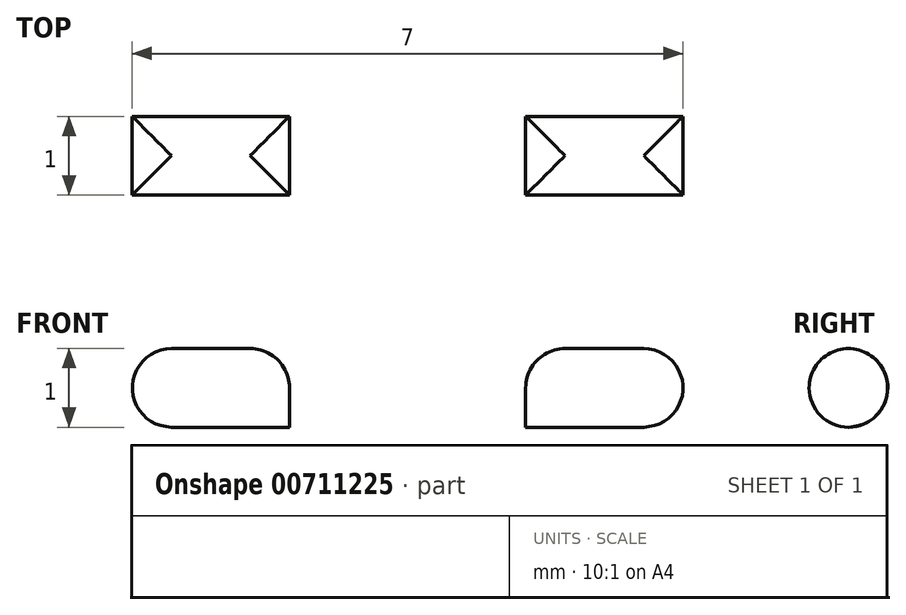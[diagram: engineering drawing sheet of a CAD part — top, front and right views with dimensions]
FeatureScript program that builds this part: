
annotation { "Feature Type Name" : "Feature", "Feature Type Description" : "" }
export const myFeature = defineFeature(function(context is Context, id is Id, definition is map)
    precondition{}
    {
        {
            var Q0;
            Q0=qCreatedBy(makeId("Top.planeOp"),FACE);
            var sketch = newSketch(context, id + "F0", { "sketchPlane" : qUnion([Q0])});
            skCircle(sketch, "E0", {"center": v(0, 0) * mm, "radius": 2.5 * mm});
            skCircle(sketch, "E1", {"center": v(0, 0) * mm, "radius": 0.5 * mm});
            skLineSegment(sketch, "E2.bottom", {"start": v(1.5, -0.5) * mm, "end": v(3.5, -0.5) * mm});
            skLineSegment(sketch, "E2.top", {"start": v(1.5, 0.5) * mm, "end": v(3.5, 0.5) * mm});
            skLineSegment(sketch, "E2.left", {"start": v(1.5, -0.5) * mm, "end": v(1.5, 0.5) * mm});
            skLineSegment(sketch, "E2.right", {"start": v(3.5, -0.5) * mm, "end": v(3.5, 0.5) * mm});
            skLineSegment(sketch, "E3.MirrorCS", {"start": v(-1.5, -0.5) * mm, "end": v(-1.5, 0.5) * mm});
            skLineSegment(sketch, "E4.MirrorCS", {"start": v(-1.5, 0.5) * mm, "end": v(-3.5, 0.5) * mm});
            skLineSegment(sketch, "E5.MirrorCS", {"start": v(-1.5, -0.5) * mm, "end": v(-3.5, -0.5) * mm});
            skLineSegment(sketch, "E6.MirrorCS", {"start": v(-3.5, -0.5) * mm, "end": v(-3.5, 0.5) * mm});
            skSolve(sketch);
        }
        {
            var Q0;
            Q0=makeQuery(id+"F0.imprint","IMPRINT",FACE,{"disambiguationData":[TD([[makeQuery(id+"F0.imprint","IMPRINT",EDGE,{"derivedFrom":sQuery(id+"F0.wireOp",EDGE,"E1")}),1.0]])]});
            var Q1;
            {var subQ5=sQuery(id+"F0.wireOp",EDGE,"E2.left");Q1=makeQuery(id+"F0.imprint","IMPRINT",FACE,{"disambiguationData":[TD([[makeQuery(id+"F0.imprint","IMPRINT",EDGE,{"derivedFrom":subQ5}),-1.0]])]});}
            var Q2;
            {var subQ5=sQuery(id+"F0.wireOp",EDGE,"E2.right");Q2=makeQuery(id+"F0.imprint","IMPRINT",FACE,{"disambiguationData":[TD([[makeQuery(id+"F0.imprint","IMPRINT",EDGE,{"derivedFrom":subQ5}),1.0]])]});}
            var Q3;
            {var subQ5=sQuery(id+"F0.wireOp",EDGE,"E6.MirrorCS");Q3=makeQuery(id+"F0.imprint","IMPRINT",FACE,{"disambiguationData":[TD([[makeQuery(id+"F0.imprint","IMPRINT",EDGE,{"derivedFrom":subQ5}),-1.0]])]});}
            var Q4;
            {var subQ5=sQuery(id+"F0.wireOp",EDGE,"E3.MirrorCS");Q4=makeQuery(id+"F0.imprint","IMPRINT",FACE,{"disambiguationData":[TD([[makeQuery(id+"F0.imprint","IMPRINT",EDGE,{"derivedFrom":subQ5}),1.0]])]});}
            extrude(context, id + "F1", {"entities" : qUnion([Q0, Q1, Q2, Q3, Q4]), "depth" : 1 * mm, "offsetDistance" : 25.4 * mm});
        }
        {
            var Q0;
            Q0=makeQuery(id+"F1.opExtrude","CAP_FACE",FACE,{"disambiguationData":[OSD([sQuery(id+"F0.wireOp",EDGE,"E0"),sQuery(id+"F0.wireOp",EDGE,"E1"),sQuery(id+"F0.wireOp",EDGE,"E2.bottom"),sQuery(id+"F0.wireOp",EDGE,"E2.top"),sQuery(id+"F0.wireOp",EDGE,"E2.right"),sQuery(id+"F0.wireOp",EDGE,"E4.MirrorCS"),sQuery(id+"F0.wireOp",EDGE,"E5.MirrorCS"),sQuery(id+"F0.wireOp",EDGE,"E6.MirrorCS")])],"isStart":false});
            var Q1;
            {var subQ0=sQuery(id+"F0.wireOp",EDGE,"E0");Q1=makeQuery(id+"F1.opExtrude","CAP_EDGE",EDGE,{"disambiguationData":[OSD([subQ0]),TDD([makeQuery(id+"F0.imprint","IMPRINT",EDGE,{"disambiguationData":[TD([[makeQuery(id+"F0.imprint","INTERSECT",VERTEX,{"derivedFrom":[subQ0,sQuery(id+"F0.wireOp",EDGE,"E2.bottom")]}),-1.0]])],"derivedFrom":subQ0})])],"isStart":false});}
            var Q2;
            {var subQ0=sQuery(id+"F0.wireOp",EDGE,"E0");Q2=makeQuery(id+"F1.opExtrude","CAP_EDGE",EDGE,{"disambiguationData":[OSD([subQ0]),TDD([makeQuery(id+"F0.imprint","IMPRINT",EDGE,{"disambiguationData":[TD([[makeQuery(id+"F0.imprint","INTERSECT",VERTEX,{"derivedFrom":[subQ0,sQuery(id+"F0.wireOp",EDGE,"E2.top")]}),1.0]])],"derivedFrom":subQ0})])],"isStart":false});}
            var Q3;
            Q3=makeQuery(id+"F1.opExtrude","CAP_EDGE",EDGE,{"disambiguationData":[OSD([sQuery(id+"F0.wireOp",EDGE,"E2.top")])],"isStart":false});
            var Q4;
            Q4=makeQuery(id+"F1.opExtrude","CAP_EDGE",EDGE,{"disambiguationData":[OSD([sQuery(id+"F0.wireOp",EDGE,"E2.right")])],"isStart":false});
            var Q5;
            Q5=makeQuery(id+"F1.opExtrude","CAP_EDGE",EDGE,{"disambiguationData":[OSD([sQuery(id+"F0.wireOp",EDGE,"E2.bottom")])],"isStart":false});
            var Q6;
            Q6=makeQuery(id+"F1.opExtrude","CAP_EDGE",EDGE,{"disambiguationData":[OSD([sQuery(id+"F0.wireOp",EDGE,"E4.MirrorCS")])],"isStart":false});
            var Q7;
            Q7=makeQuery(id+"F1.opExtrude","CAP_EDGE",EDGE,{"disambiguationData":[OSD([sQuery(id+"F0.wireOp",EDGE,"E6.MirrorCS")])],"isStart":false});
            var Q8;
            Q8=makeQuery(id+"F1.opExtrude","CAP_EDGE",EDGE,{"disambiguationData":[OSD([sQuery(id+"F0.wireOp",EDGE,"E5.MirrorCS")])],"isStart":false});
            var Q9;
            {var subQ0=sQuery(id+"F0.wireOp",EDGE,"E0");Q9=makeQuery(id+"F1.opExtrude","CAP_EDGE",EDGE,{"disambiguationData":[OSD([subQ0]),TDD([makeQuery(id+"F0.imprint","IMPRINT",EDGE,{"disambiguationData":[TD([[makeQuery(id+"F0.imprint","INTERSECT",VERTEX,{"derivedFrom":[subQ0,sQuery(id+"F0.wireOp",EDGE,"E2.bottom")]}),-1.0]])],"derivedFrom":subQ0})])],"isStart":true});}
            var Q10;
            Q10=makeQuery(id+"F1.opExtrude","CAP_EDGE",EDGE,{"disambiguationData":[OSD([sQuery(id+"F0.wireOp",EDGE,"E1")])],"isStart":true});
            var Q11;
            {var subQ0=sQuery(id+"F0.wireOp",EDGE,"E0");Q11=makeQuery(id+"F1.opExtrude","CAP_EDGE",EDGE,{"disambiguationData":[OSD([subQ0]),TDD([makeQuery(id+"F0.imprint","IMPRINT",EDGE,{"disambiguationData":[TD([[makeQuery(id+"F0.imprint","INTERSECT",VERTEX,{"derivedFrom":[subQ0,sQuery(id+"F0.wireOp",EDGE,"E2.top")]}),1.0]])],"derivedFrom":subQ0})])],"isStart":true});}
            var Q12;
            Q12=makeQuery(id+"F1.opExtrude","CAP_EDGE",EDGE,{"disambiguationData":[OSD([sQuery(id+"F0.wireOp",EDGE,"E4.MirrorCS")])],"isStart":true});
            var Q13;
            Q13=makeQuery(id+"F1.opExtrude","CAP_EDGE",EDGE,{"disambiguationData":[OSD([sQuery(id+"F0.wireOp",EDGE,"E6.MirrorCS")])],"isStart":true});
            var Q14;
            Q14=makeQuery(id+"F1.opExtrude","CAP_EDGE",EDGE,{"disambiguationData":[OSD([sQuery(id+"F0.wireOp",EDGE,"E2.right")])],"isStart":true});
            var Q15;
            Q15=makeQuery(id+"F1.opExtrude","CAP_EDGE",EDGE,{"disambiguationData":[OSD([sQuery(id+"F0.wireOp",EDGE,"E5.MirrorCS")])],"isStart":true});
            var Q16;
            Q16=makeQuery(id+"F1.opExtrude","CAP_EDGE",EDGE,{"disambiguationData":[OSD([sQuery(id+"F0.wireOp",EDGE,"E2.bottom")])],"isStart":true});
            var Q17;
            Q17=makeQuery(id+"F1.opExtrude","CAP_EDGE",EDGE,{"disambiguationData":[OSD([sQuery(id+"F0.wireOp",EDGE,"E2.top")])],"isStart":true});
            var Q18;
            Q18=makeQuery(id+"F1.opExtrude","CAP_EDGE",EDGE,{"disambiguationData":[OSD([sQuery(id+"F0.wireOp",EDGE,"E1")])],"isStart":false});
            fillet(context, id + "F2", {"entities" : qUnion([Q0, Q1, Q2, Q3, Q4, Q5, Q6, Q7, Q8, Q9, Q10, Q11, Q12, Q13, Q14, Q15, Q16, Q17, Q18]), "radius" : .5 * mm, "tangentPropagation" : true, "allowEdgeOverflow" : false});
        }
    });
